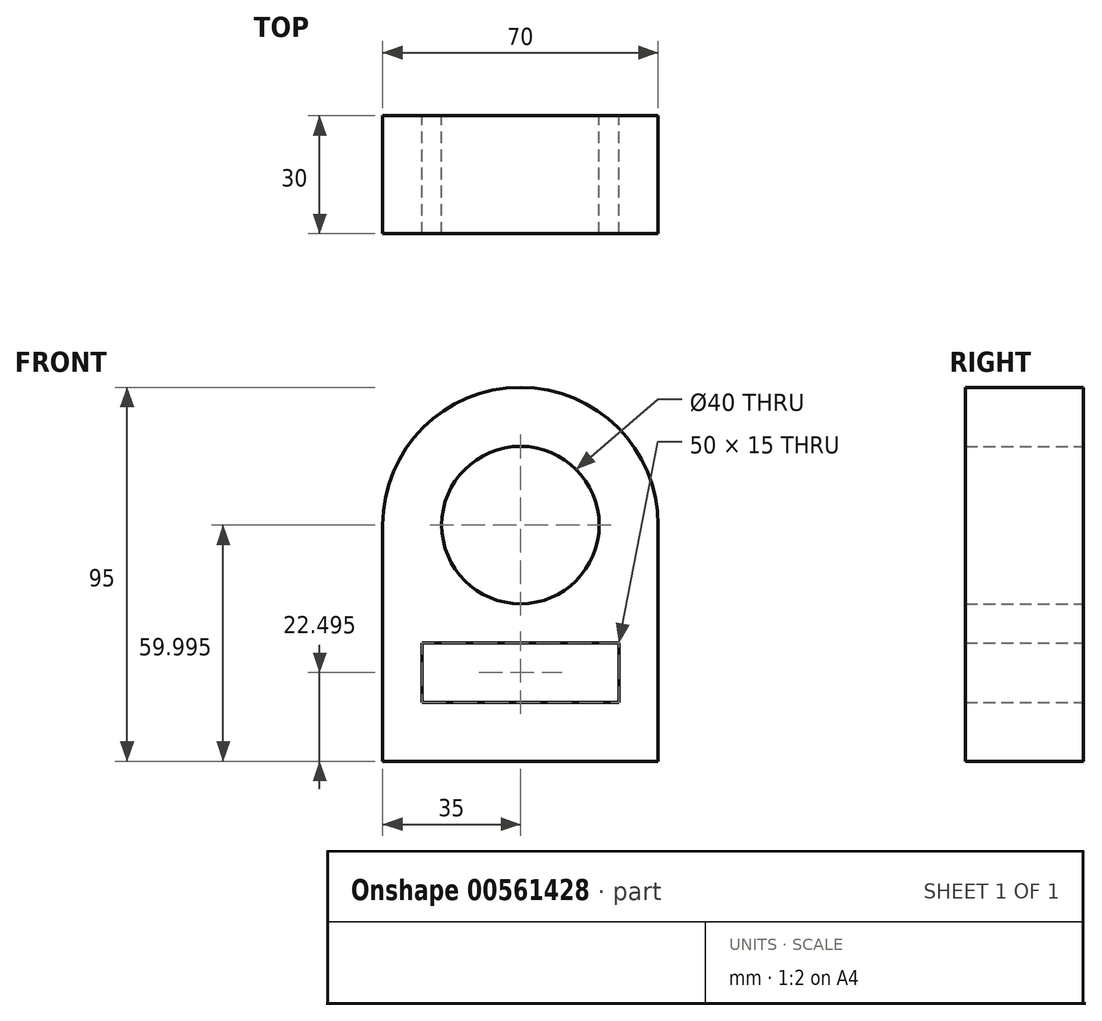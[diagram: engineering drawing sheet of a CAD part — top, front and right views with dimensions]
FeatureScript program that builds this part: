
annotation { "Feature Type Name" : "Feature", "Feature Type Description" : "" }
export const myFeature = defineFeature(function(context is Context, id is Id, definition is map)
    precondition{}
    {
        {
            var Q0;
            Q0=qCreatedBy(makeId("Front.planeOp"),FACE);
            var sketch = newSketch(context, id + "F0", { "sketchPlane" : qUnion([Q0])});
            skArc(sketch, "E0", {"start": v(35, 29.05) * mm, "mid": v(0, 64.05) * mm, "end": v(-35, 29.05) * mm});
            skCircle(sketch, "E1", {"center": v(0, 29.05) * mm, "radius": 20 * mm});
            skLineSegment(sketch, "E2", {"start": v(-35, 29.05) * mm, "end": v(-35, -30.95) * mm});
            skLineSegment(sketch, "E3", {"start": v(35, 29.05) * mm, "end": v(35, -30.95) * mm});
            skLineSegment(sketch, "E4", {"start": v(-35, -30.95) * mm, "end": v(35, -30.95) * mm});
            skLineSegment(sketch, "E5.bottom", {"start": v(-25, -0.95) * mm, "end": v(25, -0.95) * mm});
            skLineSegment(sketch, "E5.top", {"start": v(-25, -15.95) * mm, "end": v(25, -15.95) * mm});
            skLineSegment(sketch, "E5.left", {"start": v(-25, -0.95) * mm, "end": v(-25, -15.95) * mm});
            skLineSegment(sketch, "E5.right", {"start": v(25, -0.95) * mm, "end": v(25, -15.95) * mm});
            skSolve(sketch);
        }
        {
            var Q0;
            Q0=makeQuery(id+"F0.imprint","IMPRINT",FACE,{"disambiguationData":[TD([[makeQuery(id+"F0.imprint","IMPRINT",EDGE,{"derivedFrom":sQuery(id+"F0.wireOp",EDGE,"E0")}),1.0]])]});
            extrude(context, id + "F1", {"entities" : qUnion([Q0]), "depth" : 30 * mm, "offsetDistance" : 25 * mm});
        }
    });
